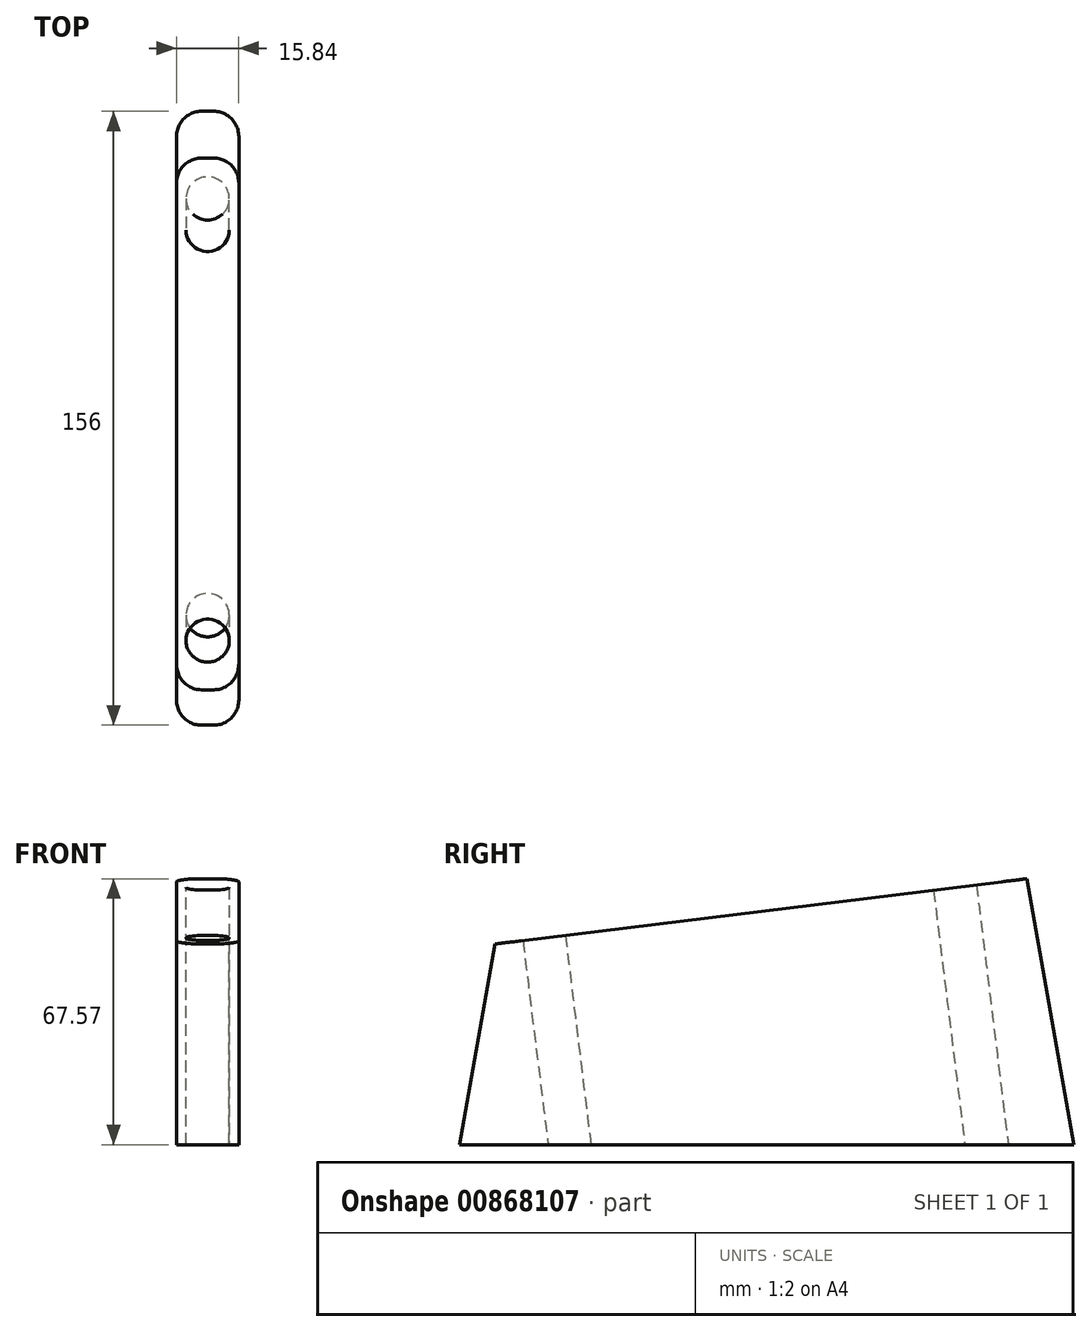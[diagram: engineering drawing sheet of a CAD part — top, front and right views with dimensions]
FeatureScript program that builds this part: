
annotation { "Feature Type Name" : "Feature", "Feature Type Description" : "" }
export const myFeature = defineFeature(function(context is Context, id is Id, definition is map)
    precondition{}
    {
        {
            var Q0;
            Q0=qCreatedBy(makeId("Right.planeOp"),FACE);
            var sketch = newSketch(context, id + "F0", { "sketchPlane" : qUnion([Q0])});
            skLineSegment(sketch, "E0", {"start": v(0, 0) * mm, "end": v(-156, 0) * mm});
            skLineSegment(sketch, "E1", {"start": v(-156, 0) * mm, "end": v(-147.01, 50.98) * mm});
            skLineSegment(sketch, "E2", {"start": v(0, 0) * mm, "end": v(-11.91, 67.57) * mm});
            skLineSegment(sketch, "E3", {"start": v(-147.01, 50.98) * mm, "end": v(-11.91, 67.57) * mm});
            skLineSegment(sketch, "E4", {"start": v(-134.5, 52.52) * mm, "end": v(-128.05, 0) * mm, "construction": true});
            skLineSegment(sketch, "E5", {"start": v(-30.18, 65.33) * mm, "end": v(-22.16, 0) * mm, "construction": true});
            skSolve(sketch);
        }
        {
            var Q0;
            Q0=makeQuery(id+"F0.imprint","IMPRINT",FACE,{"disambiguationData":[TD([[makeQuery(id+"F0.imprint","IMPRINT",EDGE,{"derivedFrom":sQuery(id+"F0.wireOp",EDGE,"E0")}),-1.0]])]});
            extrude(context, id + "F1", {"entities" : qUnion([Q0]), "depth" : 15.85 * mm, "offsetDistance" : 25 * mm, "symmetric" : true});
        }
        {
            var Q0;
            Q0=makeQuery(id+"F1.opExtrude","CAP_EDGE",EDGE,{"disambiguationData":[OSD([sQuery(id+"F0.wireOp",EDGE,"E1")])],"isStart":false});
            var Q1;
            Q1=makeQuery(id+"F1.opExtrude","CAP_EDGE",EDGE,{"disambiguationData":[OSD([sQuery(id+"F0.wireOp",EDGE,"E1")])],"isStart":true});
            var Q2;
            Q2=makeQuery(id+"F1.opExtrude","CAP_EDGE",EDGE,{"disambiguationData":[OSD([sQuery(id+"F0.wireOp",EDGE,"E2")])],"isStart":false});
            var Q3;
            Q3=makeQuery(id+"F1.opExtrude","CAP_EDGE",EDGE,{"disambiguationData":[OSD([sQuery(id+"F0.wireOp",EDGE,"E2")])],"isStart":true});
            fillet(context, id + "F2", {"entities" : qUnion([Q0, Q1, Q2, Q3]), "radius" : 6.35 * mm, "tangentPropagation" : true, "allowEdgeOverflow" : false});
        }
        {
            var Q0;
            Q0=makeQuery(id+"F1.opExtrude","SWEPT_FACE",FACE,{"disambiguationData":[OSD([sQuery(id+"F0.wireOp",EDGE,"E3")])]});
            var sketch = newSketch(context, id + "F3", { "sketchPlane" : qUnion([Q0])});
            skCircle(sketch, "E6", {"center": v(0, -127.1) * mm, "radius": 5.5 * mm});
            skSolve(sketch);
        }
        {
            var Q0;
            Q0=makeQuery(id+"F1.opExtrude","SWEPT_FACE",FACE,{"disambiguationData":[OSD([sQuery(id+"F0.wireOp",EDGE,"E0")])]});
            var sketch = newSketch(context, id + "F4", { "sketchPlane" : qUnion([Q0])});
            skCircle(sketch, "E7", {"center": v(0, 128.05) * mm, "radius": 5.5 * mm});
            skSolve(sketch);
        }
        {
            var Q1;
            Q1 = qSketchRegion(id + "F3", true);
            var Q2;
            Q2 = qSketchRegion(id + "F4", true);
            loft(context, id + "F5", {"operationType" : NewBodyOperationType.REMOVE, "sheetProfilesArray" : [{ "sheetProfileEntities" : qUnion([Q1]) }, { "sheetProfileEntities" : qUnion([Q2]) }]});
        }
        {
            var Q0;
            Q0=makeQuery(id+"F1.opExtrude","SWEPT_FACE",FACE,{"disambiguationData":[OSD([sQuery(id+"F0.wireOp",EDGE,"E0")])]});
            var sketch = newSketch(context, id + "F6", { "sketchPlane" : qUnion([Q0])});
            skCircle(sketch, "E8", {"center": v(0, 22.16) * mm, "radius": 5.5 * mm});
            skSolve(sketch);
        }
        {
            var Q0;
            Q0=makeQuery(id+"F1.opExtrude","SWEPT_FACE",FACE,{"disambiguationData":[OSD([sQuery(id+"F0.wireOp",EDGE,"E3")])]});
            var sketch = newSketch(context, id + "F7", { "sketchPlane" : qUnion([Q0])});
            skCircle(sketch, "E9", {"center": v(0, -22) * mm, "radius": 5.5 * mm});
            skSolve(sketch);
        }
        {
            var Q1;
            Q1 = qSketchRegion(id + "F6", true);
            var Q2;
            Q2 = qSketchRegion(id + "F7", true);
            loft(context, id + "F8", {"operationType" : NewBodyOperationType.REMOVE, "sheetProfilesArray" : [{ "sheetProfileEntities" : qUnion([Q1]) }, { "sheetProfileEntities" : qUnion([Q2]) }]});
        }
    });
